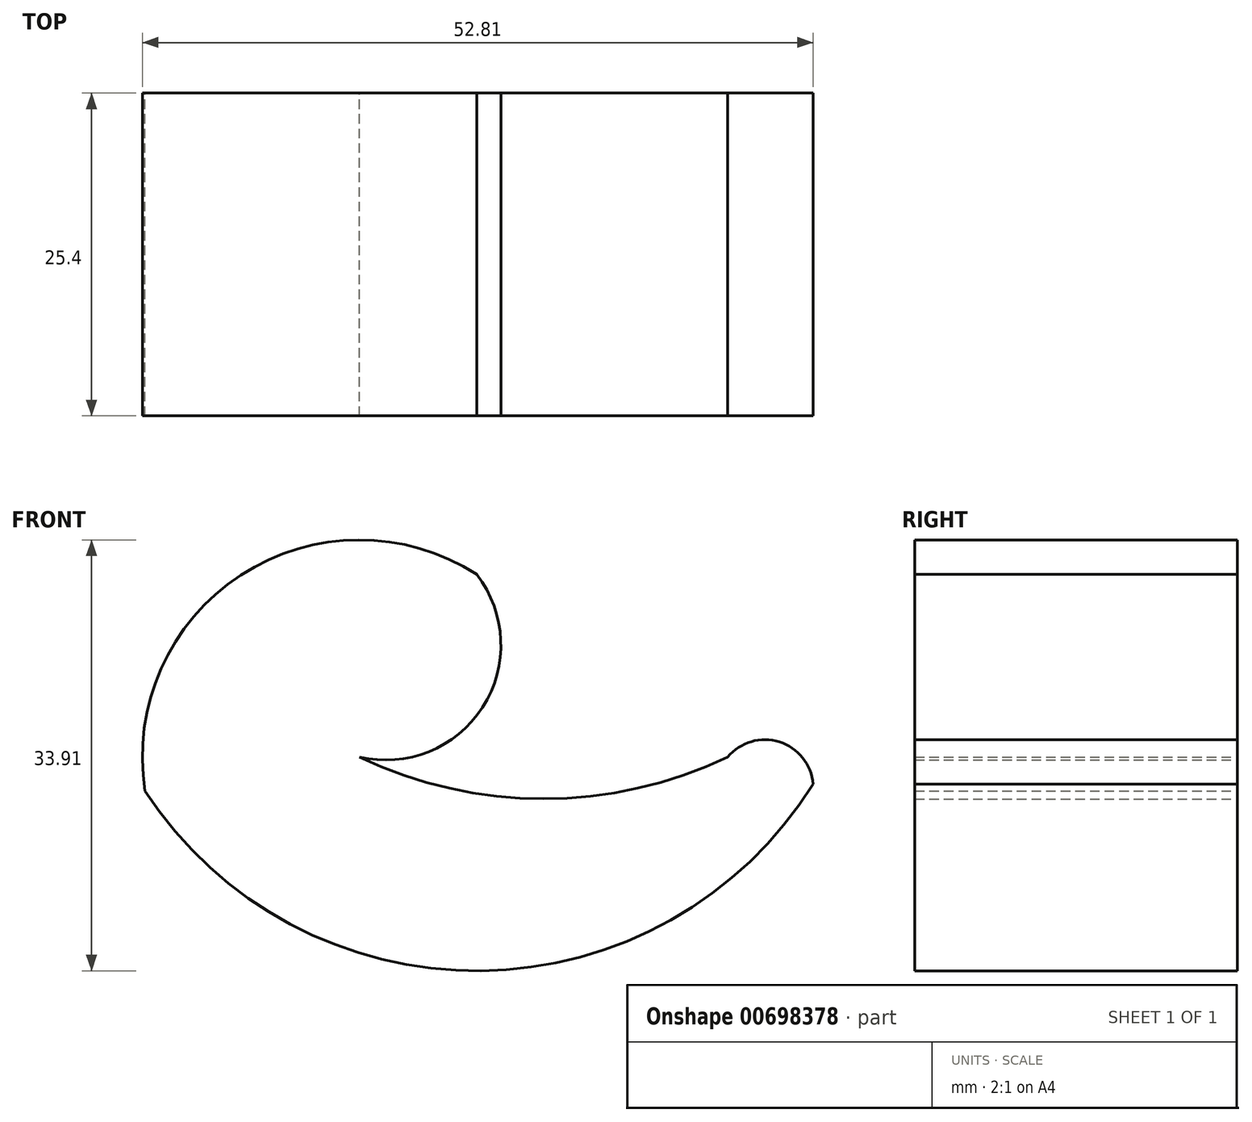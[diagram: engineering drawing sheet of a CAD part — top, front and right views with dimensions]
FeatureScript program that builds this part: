
annotation { "Feature Type Name" : "Feature", "Feature Type Description" : "" }
export const myFeature = defineFeature(function(context is Context, id is Id, definition is map)
    precondition{}
    {
        {
            var Q0;
            Q0=qCreatedBy(makeId("Front.planeOp"),FACE);
            var sketch = newSketch(context, id + "F0", { "sketchPlane" : qUnion([Q0])});
            skArc(sketch, "E0", {"start": v(-40.14, -16.37) * mm, "mid": v(-13.7, -30.5) * mm, "end": v(12.45, -15.8) * mm});
            skArc(sketch, "E1", {"start": v(-14.03, 0.68) * mm, "mid": v(-32.61, 0.62) * mm, "end": v(-40.14, -16.37) * mm});
            skArc(sketch, "E2", {"start": v(-23.28, -13.68) * mm, "mid": v(-13.57, -9.78) * mm, "end": v(-14.03, 0.68) * mm});
            skArc(sketch, "E3", {"start": v(-23.28, -13.68) * mm, "mid": v(-8.77, -16.98) * mm, "end": v(5.73, -13.68) * mm});
            skArc(sketch, "E4", {"start": v(12.45, -15.8) * mm, "mid": v(9.8, -12.5) * mm, "end": v(5.73, -13.68) * mm});
            skSolve(sketch);
        }
        {
            var Q0;
            Q0=makeQuery(id+"F0.imprint","IMPRINT",FACE,{"disambiguationData":[TD([[makeQuery(id+"F0.imprint","IMPRINT",EDGE,{"derivedFrom":sQuery(id+"F0.wireOp",EDGE,"E0")}),1.0]])]});
            extrude(context, id + "F1", {"entities" : qUnion([Q0]), "depth" : 25.4 * mm, "offsetDistance" : 25.4 * mm});
        }
    });
